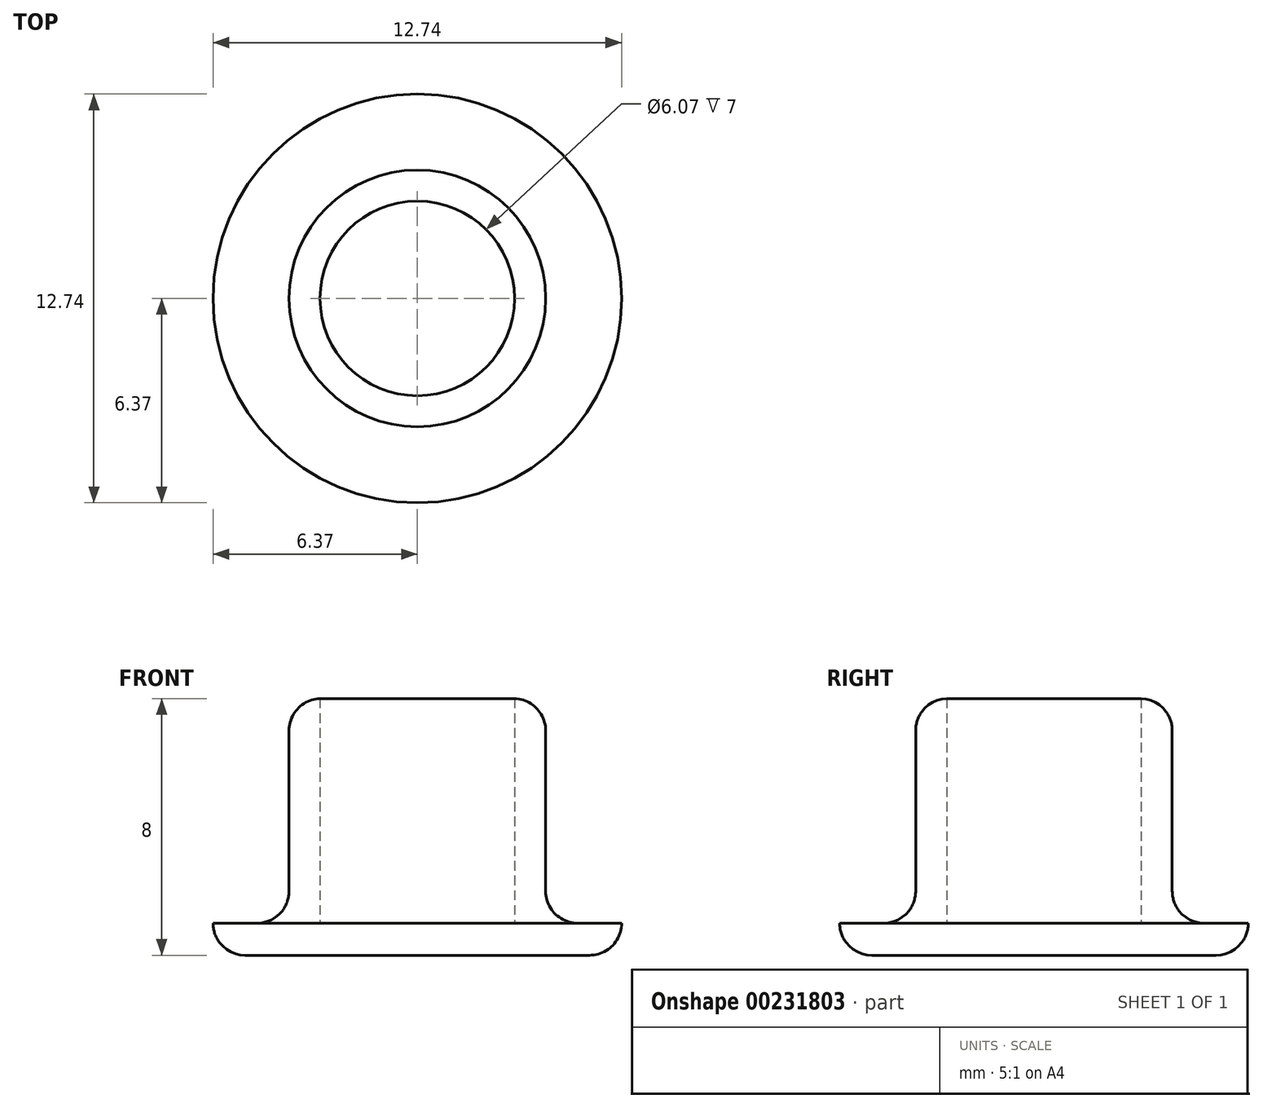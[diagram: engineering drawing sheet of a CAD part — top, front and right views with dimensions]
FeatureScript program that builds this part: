
annotation { "Feature Type Name" : "Feature", "Feature Type Description" : "" }
export const myFeature = defineFeature(function(context is Context, id is Id, definition is map)
    precondition{}
    {
        {
            var Q0;
            Q0=qCreatedBy(makeId("Top.planeOp"),FACE);
            var sketch = newSketch(context, id + "F0", { "sketchPlane" : qUnion([Q0])});
            skCircle(sketch, "E0", {"center": v(0, 0) * mm, "radius": 4 * mm});
            skSolve(sketch);
        }
        {
            var Q0;
            Q0 = qSketchRegion(id + "F0", true);
            extrude(context, id + "F1", {"entities" : qUnion([Q0]), "depth" : 8 * mm});
        }
        {
            var Q0;
            Q0=qCreatedBy(makeId("Top.planeOp"),FACE);
            var sketch = newSketch(context, id + "F2", { "sketchPlane" : qUnion([Q0])});
            skCircle(sketch, "E1", {"center": v(0, 0) * mm, "radius": 3.03 * mm});
            skSolve(sketch);
        }
        {
            var Q0;
            Q0 = qSketchRegion(id + "F2", true);
            extrude(context, id + "F3", {"entities" : qUnion([Q0]), "operationType" : NewBodyOperationType.REMOVE, "depth" : 9.4 * mm});
        }
        {
            var Q0;
            Q0=qCreatedBy(makeId("Top.planeOp"),FACE);
            var sketch = newSketch(context, id + "F4", { "sketchPlane" : qUnion([Q0])});
            skCircle(sketch, "E2", {"center": v(0, 0) * mm, "radius": 6.37 * mm});
            skSolve(sketch);
        }
        {
            var Q0;
            Q0=makeQuery(id+"F4.imprint","IMPRINT",FACE,{"disambiguationData":[TD([[makeQuery(id+"F4.imprint","IMPRINT",EDGE,{"derivedFrom":sQuery(id+"F4.wireOp",EDGE,"E2")}),1.0]])]});
            extrude(context, id + "F5", {"entities" : qUnion([Q0]), "operationType" : NewBodyOperationType.ADD, "depth" : 1 * mm});
        }
        {
            var Q0;
            Q0=makeQuery(id+"F5.boolean.opBoolean","INTERSECT",EDGE,{"derivedFrom":[makeQuery(id+"F1.opExtrude","SWEPT_FACE",FACE,{"disambiguationData":[OSD([sQuery(id+"F0.wireOp",EDGE,"E0")])]}),makeQuery(id+"F5.opExtrude","CAP_FACE",FACE,{"disambiguationData":[OSD([sQuery(id+"F4.wireOp",EDGE,"E2")])],"isStart":false})]});
            fillet(context, id + "F6", {"entities" : qUnion([Q0]), "radius" : 1 * mm, "tangentPropagation" : true, "allowEdgeOverflow" : false});
        }
        {
            var Q0;
            Q0=makeQuery(id+"F5.opExtrude","CAP_EDGE",EDGE,{"disambiguationData":[OSD([sQuery(id+"F4.wireOp",EDGE,"E2")])],"isStart":true});
            var Q1;
            Q1=makeQuery(id+"F1.opExtrude","CAP_EDGE",EDGE,{"disambiguationData":[OSD([sQuery(id+"F0.wireOp",EDGE,"E0")])],"isStart":false});
            fillet(context, id + "F7", {"entities" : qUnion([Q0, Q1]), "radius" : 1 * mm, "tangentPropagation" : true, "allowEdgeOverflow" : false});
        }
    });
